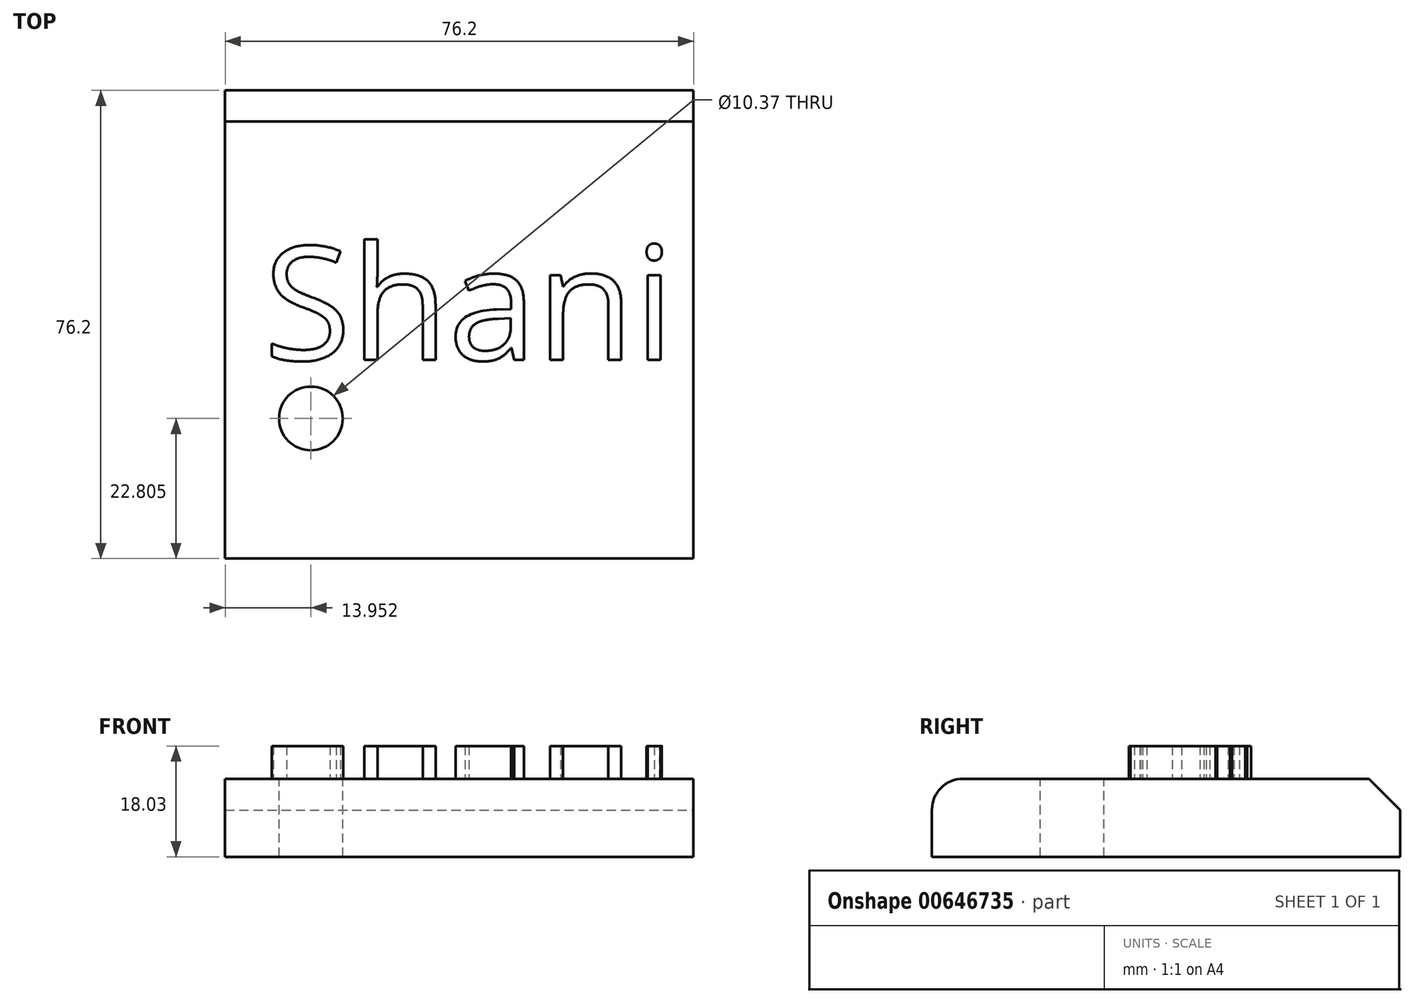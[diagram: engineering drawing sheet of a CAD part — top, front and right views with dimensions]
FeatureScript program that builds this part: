
annotation { "Feature Type Name" : "Feature", "Feature Type Description" : "" }
export const myFeature = defineFeature(function(context is Context, id is Id, definition is map)
    precondition{}
    {
        {
            var Q0;
            Q0=qCreatedBy(makeId("Top.planeOp"),FACE);
            var sketch = newSketch(context, id + "F0", { "sketchPlane" : qUnion([Q0])});
            skLineSegment(sketch, "E0.bottom", {"start": v(-50.17, 47.27) * mm, "end": v(26.03, 47.27) * mm});
            skLineSegment(sketch, "E0.top", {"start": v(-50.17, -28.93) * mm, "end": v(26.03, -28.93) * mm});
            skLineSegment(sketch, "E0.left", {"start": v(-50.17, 47.27) * mm, "end": v(-50.17, -28.93) * mm});
            skLineSegment(sketch, "E0.right", {"start": v(26.03, 47.27) * mm, "end": v(26.03, -28.93) * mm});
            skSolve(sketch);
        }
        {
            var Q0;
            Q0=makeQuery(id+"F0.imprint","IMPRINT",FACE,{"disambiguationData":[TD([[makeQuery(id+"F0.imprint","IMPRINT",EDGE,{"derivedFrom":sQuery(id+"F0.wireOp",EDGE,"E0.bottom")}),-1.0]])]});
            extrude(context, id + "F1", {"entities" : qUnion([Q0]), "depth" : 12.7 * mm, "offsetDistance" : 25.4 * mm});
        }
        {
            var Q0;
            Q0=makeQuery(id+"F1.opExtrude","CAP_FACE",FACE,{"disambiguationData":[OSD([sQuery(id+"F0.wireOp",EDGE,"E0.bottom"),sQuery(id+"F0.wireOp",EDGE,"E0.top"),sQuery(id+"F0.wireOp",EDGE,"E0.left"),sQuery(id+"F0.wireOp",EDGE,"E0.right")])],"isStart":false});
            var sketch = newSketch(context, id + "F2", { "sketchPlane" : qUnion([Q0])});
            skText(sketch, "E1", { "text": "Shani", "fontName": "OpenSans-Regular.ttf"});
            const initialGuessF2  = {"E1": [-0.0439, 0.0034, 1, 0, 0.0186]};
            skSetInitialGuess(sketch, initialGuessF2);
            skSolve(sketch);
        }
        {
            var Q0;
            Q0 = qSketchRegion(id + "F2", true);
            extrude(context, id + "F3", {"entities" : qUnion([Q0]), "operationType" : NewBodyOperationType.ADD, "depth" : 5.33 * mm, "offsetDistance" : 25.4 * mm});
        }
        {
            var Q0;
            Q0=makeQuery(id+"F1.opExtrude","CAP_EDGE",EDGE,{"disambiguationData":[OSD([sQuery(id+"F0.wireOp",EDGE,"E0.top")])],"isStart":false});
            fillet(context, id + "F4", {"entities" : qUnion([Q0]), "radius" : 5.08 * mm, "tangentPropagation" : true, "allowEdgeOverflow" : false});
        }
        {
            var Q0;
            {var subQ0=sQuery(id+"F0.wireOp",EDGE,"E0.left");var subQ1=sQuery(id+"F0.wireOp",EDGE,"E0.bottom");var subQ2=sQuery(id+"F0.wireOp",EDGE,"E0.right");var subQ3=sQuery(id+"F0.wireOp",EDGE,"E0.top");Q0=makeQuery(id+"F3.boolean.opBoolean","SPLIT",FACE,{"disambiguationData":[TD([makeQuery(id+"F1.opExtrude","SWEPT_FACE",FACE,{"disambiguationData":[OSD([subQ1])]})])],"derivedFrom":makeQuery(id+"F1.opExtrude","CAP_FACE",FACE,{"disambiguationData":[OSD([subQ1,subQ3,subQ0,subQ2])],"isStart":false})});}
            var sketch = newSketch(context, id + "F5", { "sketchPlane" : qUnion([Q0])});
            skCircle(sketch, "E2", {"center": v(-36.22, -6.12) * mm, "radius": 5.19 * mm});
            skSolve(sketch);
        }
        {
            var Q0;
            Q0 = qSketchRegion(id + "F5", true);
            extrude(context, id + "F6", {"entities" : qUnion([Q0]), "operationType" : NewBodyOperationType.REMOVE, "oppositeDirection" : true, "depth" : 25.4 * mm, "offsetDistance" : 25.4 * mm});
        }
        {
            var Q0;
            Q0=makeQuery(id+"F1.opExtrude","CAP_EDGE",EDGE,{"disambiguationData":[OSD([sQuery(id+"F0.wireOp",EDGE,"E0.bottom")])],"isStart":false});
            chamfer(context, id + "F7", {"entities" : qUnion([Q0]), "width" : 5.08 * mm, "tangentPropagation" : true});
        }
    });
